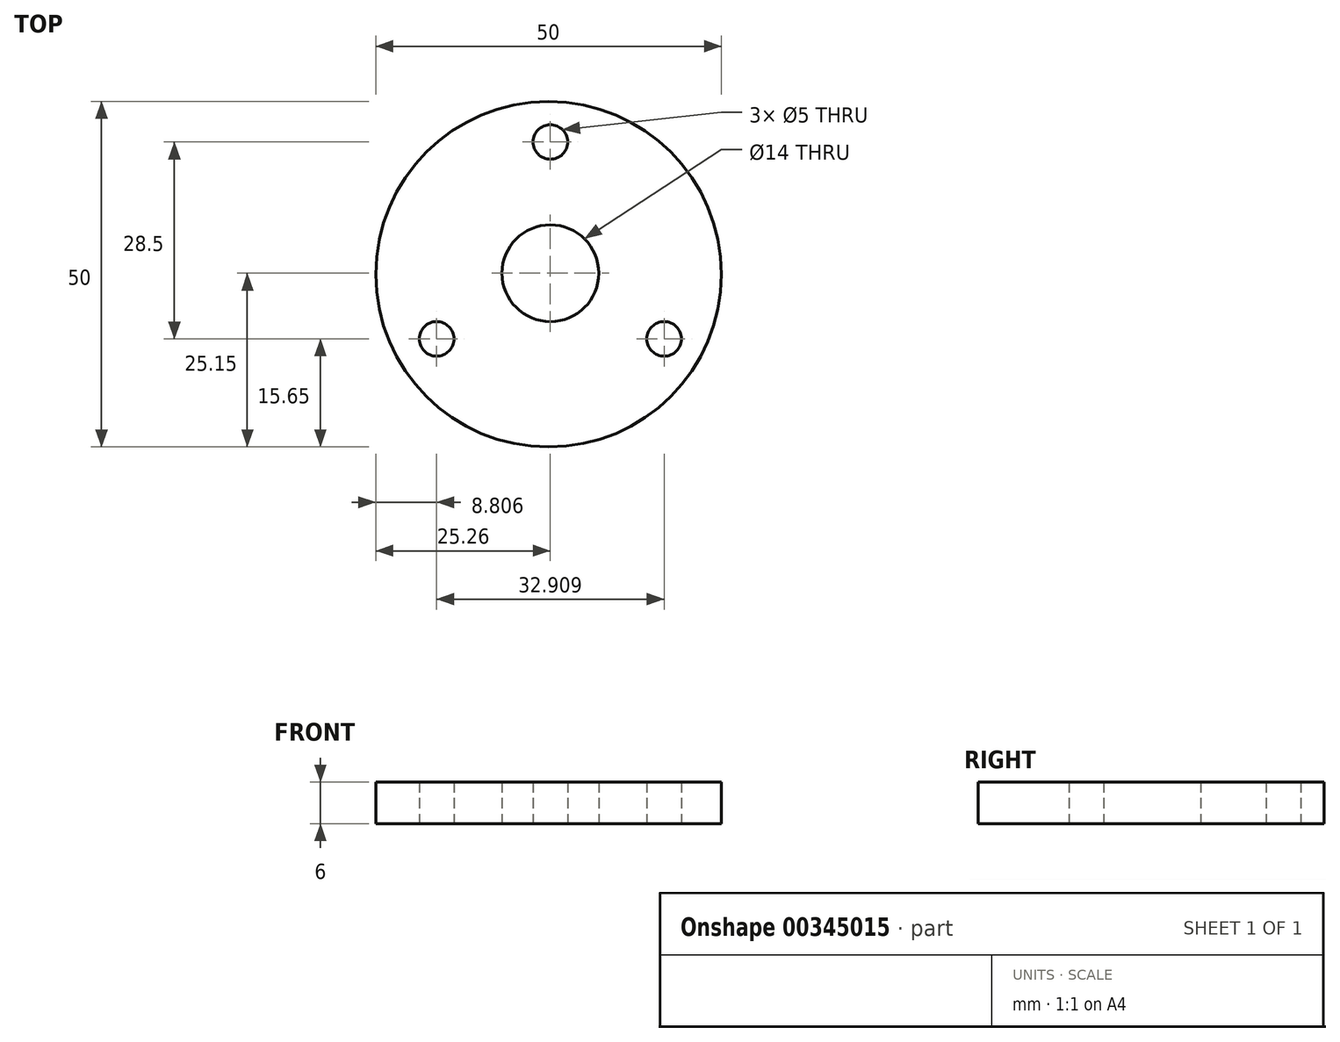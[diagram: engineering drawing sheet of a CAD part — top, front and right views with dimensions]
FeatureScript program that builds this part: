
annotation { "Feature Type Name" : "Feature", "Feature Type Description" : "" }
export const myFeature = defineFeature(function(context is Context, id is Id, definition is map)
    precondition{}
    {
        {
            var Q0;
            Q0=qCreatedBy(makeId("Top.planeOp"),FACE);
            var sketch = newSketch(context, id + "F0", { "sketchPlane" : qUnion([Q0])});
            skCircle(sketch, "E0", {"center": v(0, 0) * mm, "radius": 7 * mm});
            skCircle(sketch, "E1", {"center": v(0, 19) * mm, "radius": 2.5 * mm});
            skCircle(sketch, "E2", {"center": v(-16.45, -9.5) * mm, "radius": 2.5 * mm});
            skLineSegment(sketch, "E3", {"start": v(0, 7) * mm, "end": v(0, 7.8) * mm, "construction": true});
            skLineSegment(sketch, "E4", {"start": v(0, 0) * mm, "end": v(-0.26, -0.15) * mm, "construction": true});
            skCircle(sketch, "E5", {"center": v(16.45, -9.5) * mm, "radius": 2.5 * mm});
            skLineSegment(sketch, "E6", {"start": v(0, 0) * mm, "end": v(0, 7.8) * mm});
            skCircle(sketch, "E7", {"center": v(-0.26, -0.15) * mm, "radius": 25 * mm});
            skLineSegment(sketch, "E8.trimOffspring", {"start": v(0, 16.5) * mm, "end": v(0, 19) * mm});
            skSolve(sketch);
        }
        {
            var Q0;
            Q0=makeQuery(id+"F0.imprint","IMPRINT",FACE,{"disambiguationData":[TD([[makeQuery(id+"F0.imprint","IMPRINT",EDGE,{"derivedFrom":sQuery(id+"F0.wireOp",EDGE,"E0")}),-1.0]])]});
            extrude(context, id + "F1", {"entities" : qUnion([Q0]), "depth" : 6 * mm});
        }
    });
